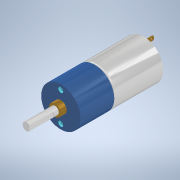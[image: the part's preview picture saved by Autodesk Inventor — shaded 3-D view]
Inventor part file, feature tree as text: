
AUTODESK INVENTOR PART (.ipt)
format: ipt  version: 2020.2 (Build 242310000, 310)  size: 200,192 bytes
history: native  units: mm
features: sketch x7, extrude x6, revolve x1
ambient origin geometry x8: Origin, YZ Plane, XZ Plane, XY Plane, X Axis, Y Axis, Z Axis, Center Point
bodies: Solid1 (feature_tree)
feature tree (14):
  extrude  "Extrusion1"  Depth=17.3mm TaperAngle=0.0deg
  extrude  "Extrusion2"  Depth=2.5mm
  extrude  "Extrusion3"  Depth=2.5mm
  extrude  "Extrusion4"  Depth=1.0mm
  extrude  "Extrusion5"  Depth=4.0mm
  revolve  "Revolution1"  [1 undecoded]
  extrude  "Extrusion6"  Depth=4.0mm
  sketch  "Sketch1"  dims[d0=20.0mm d1=17.3mm d2=0.0mm]
  sketch  "Sketch2"  dims[d3=7.5mm d4=2.5mm]
  sketch  "Sketch3"  dims[d5=7.5mm d6=2.5mm]
  sketch  "Sketch4"  dims[d7=1.0mm d8=0.0mm d9=6.0mm]
  sketch  "Sketch5"  dims[d10=3.0mm d11=0.0mm d12=4.0mm]
  sketch  "Sketch7"  dims[d13=14.5mm d14=0.0mm d15=2.0mm]
  sketch  "Sketch8"  dims[d16=0.5mm d17=4.0mm d18=12.2mm d19=0.0mm d20=10.0mm d21=25.0mm d22=1.0mm d23=3.0mm d24=3.0mm d25=120.0deg d26=90.0deg d27=8.0mm d28=5.0mm d29=2.0mm d30=0.5mm d31=4.0mm d32=1.0mm d33=7.0mm d34=0.5mm d35=0.0mm]
note: 1 required parameter value undecoded (feature->parameter linkage not recoverable at this tier; creation-order binding heuristic only, values carry confidence <= 0.55)
